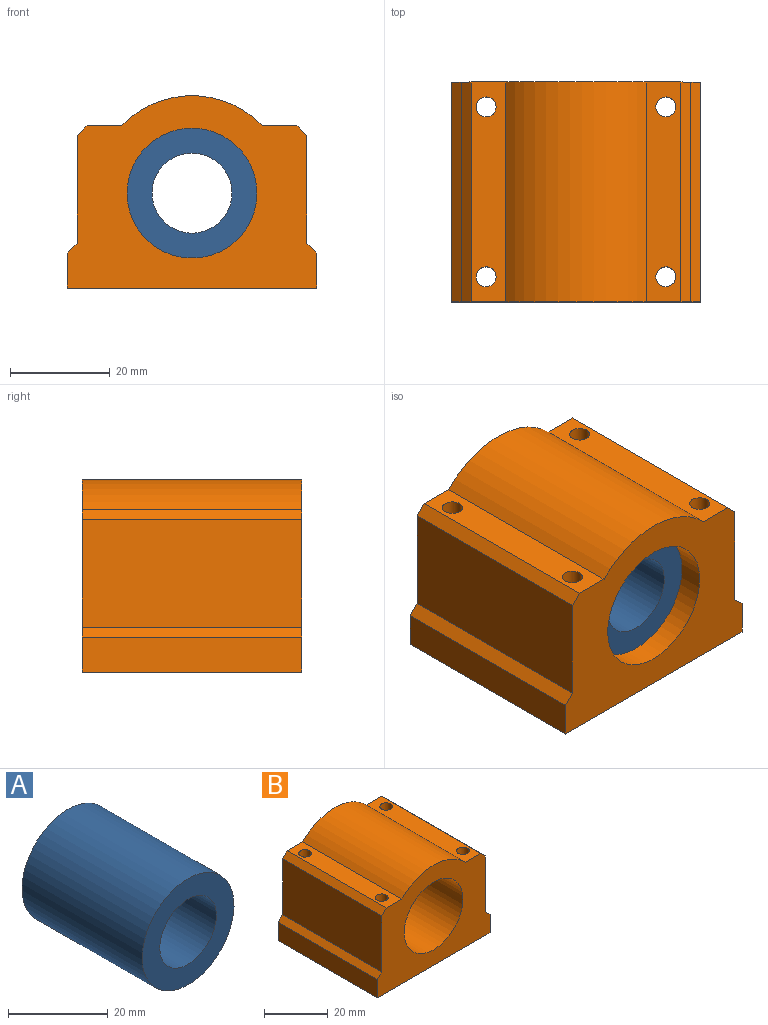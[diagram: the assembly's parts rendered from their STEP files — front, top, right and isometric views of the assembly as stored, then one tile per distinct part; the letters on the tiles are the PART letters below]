
ASSEMBLY  parts=2 mates=1
PART A: 4 faces, bbox 26x34x26 mm
  f0: plane 26x26mm, normal (0,-1,0), area 329.9mm2, adj f1,f2
  f1: cylinder r=8mm len=34mm, axis (0,1,0), area 1709mm2, adj f0,f3
  f2: cylinder r=13mm len=34mm, axis (0,1,0), area 2777.2mm2, adj f0,f3
  f3: plane 26x26mm, normal (0,1,0), area 329.9mm2, adj f1,f2
PART B: 27 faces, bbox 50x44x38.5 mm
  f0: cylinder r=2mm len=20.5mm, axis (0,0,-1), area 257.6mm2, adj f12,f25
  f1: cylinder r=2mm len=20.5mm, axis (0,0,-1), area 257.6mm2, adj f12,f23
  f2: cylinder r=2mm len=20.5mm, axis (0,0,-1), area 257.6mm2, adj f4,f21
  f3: cylinder r=2mm len=20.5mm, axis (0,0,-1), area 257.6mm2, adj f4,f19
  f4: plane 44x6.93mm, normal (0,0,1), area 279.7mm2, adj f2,f3,f6,f8,f13,f14
  f5: plane 44x7mm, normal (-1,0,0), area 308mm2, adj f6,f8,f9,f17
  f6: plane 50x38.5mm, normal (0,-1,0), area 1108.6mm2, adj f4,f5,f7,f9,f10,f11,f12,f13
  f7: plane 44x7mm, normal (1,0,0), area 308mm2, adj f6,f8,f9,f16
  f8: plane 50x38.5mm, normal (0,1,0), area 1108.6mm2, adj f4,f5,f7,f9,f10,f11,f12,f13
  f9: plane 50x44mm, normal (0,0,-1), area 2121.5mm2, adj f5,f6,f7,f8,f20,f22,f24,f26
  f10: plane 44x21.5mm, normal (-1,0,0), area 946mm2, adj f6,f8,f14,f17
  f11: plane 44x21.5mm, normal (1,0,0), area 946mm2, adj f6,f8,f15,f16
  f12: plane 44x6.93mm, normal (0,0,1), area 279.7mm2, adj f0,f1,f6,f8,f13,f15
  f13: cylinder r=19.5mm len=44mm, axis (0,1,0), area 1383.3mm2, adj f4,f6,f8,f12
  f14: plane 44x2mm, normal (-0.71,0,0.71), area 124.5mm2, adj f4,f6,f8,f10
  f15: plane 44x2mm, normal (0.71,0,0.71), area 124.5mm2, adj f6,f8,f11,f12
  f16: plane 44x2mm, normal (0.71,0,0.71), area 124.5mm2, adj f6,f7,f8,f11
  f17: plane 44x2mm, normal (-0.71,0,0.71), area 124.5mm2, adj f5,f6,f8,f10
  f18: cylinder r=13mm len=44mm, axis (0,1,0), area 3594mm2, adj f6,f8
  f19: plane 5x5mm, normal (0,0,-1), area 7.1mm2, adj f3,f20
  f20: cylinder r=2.5mm len=12mm, axis (0,0,-1), area 188.5mm2, adj f9,f19
  f21: plane 5x5mm, normal (0,0,-1), area 7.1mm2, adj f2,f22
  f22: cylinder r=2.5mm len=12mm, axis (0,0,-1), area 188.5mm2, adj f9,f21
  f23: plane 5x5mm, normal (0,0,-1), area 7.1mm2, adj f1,f24
  f24: cylinder r=2.5mm len=12mm, axis (0,0,-1), area 188.5mm2, adj f9,f23
  f25: plane 5x5mm, normal (0,0,-1), area 7.1mm2, adj f0,f26
  f26: cylinder r=2.5mm len=12mm, axis (0,0,-1), area 188.5mm2, adj f9,f25
PLACE A t=(-2.92,10.7,-0.67)mm
PLACE B t=(-2.92,10.7,-0.67)mm
MATE fastened A.f1 <-> B.f18  axis (0,-1,0) through (-2.92,-11.3,18.33)mm
